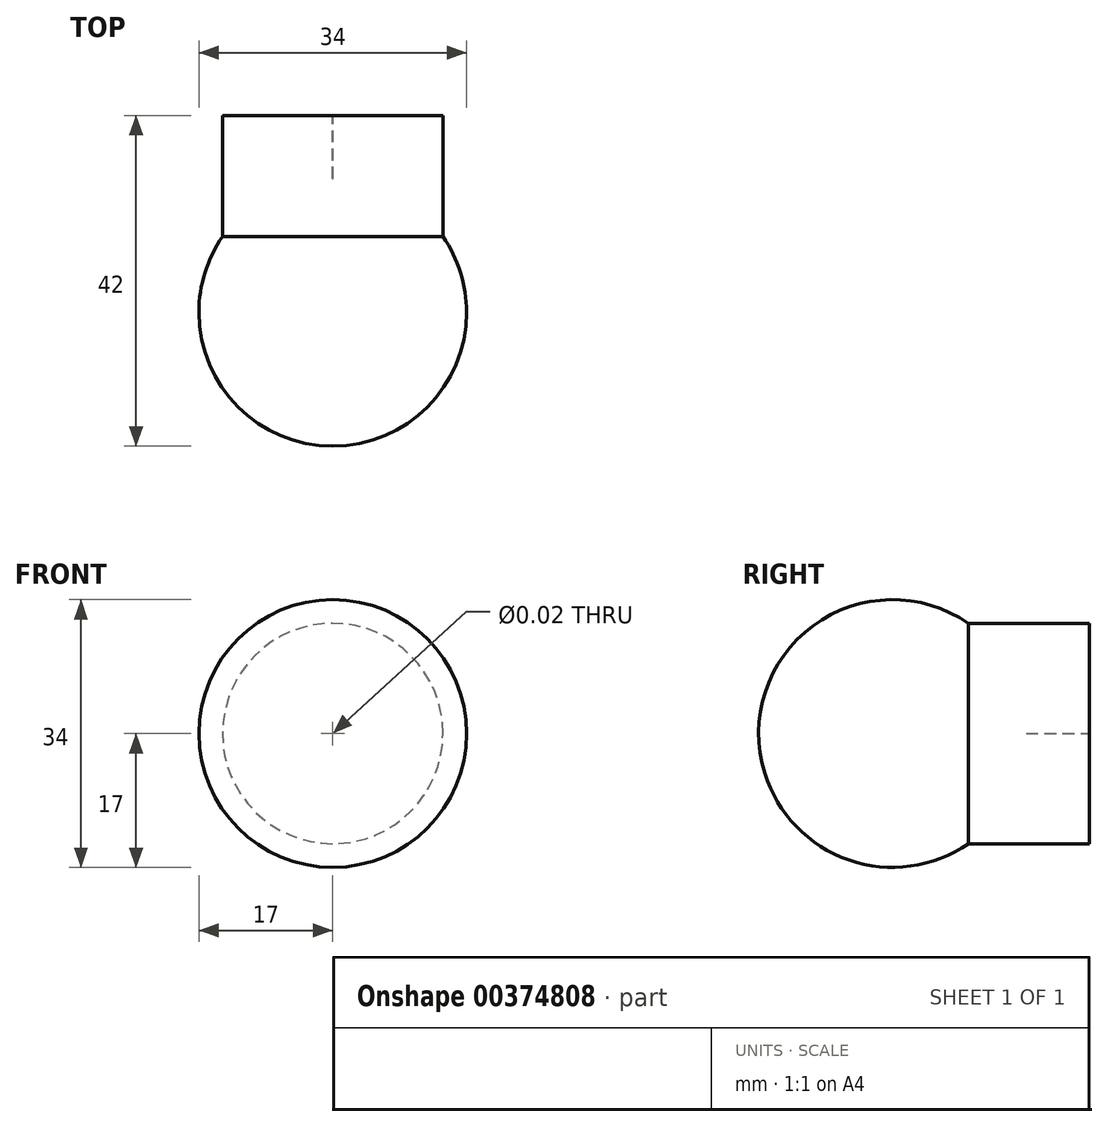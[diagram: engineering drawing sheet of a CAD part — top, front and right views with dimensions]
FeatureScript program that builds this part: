
annotation { "Feature Type Name" : "Feature", "Feature Type Description" : "" }
export const myFeature = defineFeature(function(context is Context, id is Id, definition is map)
    precondition{}
    {
        {
            var Q0;
            Q0=qCreatedBy(makeId("Front.planeOp"),FACE);
            var sketch = newSketch(context, id + "F0", { "sketchPlane" : qUnion([Q0])});
            skCircle(sketch, "E0", {"center": v(0, 0) * mm, "radius": 14 * mm});
            skCircle(sketch, "E1", {"center": v(0, 0) * mm, "radius": 11.6 * mm});
            skSolve(sketch);
        }
        {
            var Q0;
            Q0 = qSketchRegion(id + "F0", true);
            var Q1;
            Q1=makeQuery(id+"F0.imprint","IMPRINT",FACE,{"disambiguationData":[TD([[makeQuery(id+"F0.imprint","IMPRINT",EDGE,{"derivedFrom":sQuery(id+"F0.wireOp",EDGE,"E1")}),1.0]])]});
            extrude(context, id + "F1", {"entities" : qUnion([Q0, Q1]), "depth" : 25 * mm});
        }
        {
            var Q0;
            Q0=sQuery(id+"F0.wireOp",VERTEX,"E0.center");
            var Q1;
            Q1=makeQuery(id+"F1.opExtrude","SWEPT_BODY",BODY,{"disambiguationData":[OSD([sQuery(id+"F0.wireOp",EDGE,"E0")])]});
            hole(context, id + "F2", {"style" : HoleStyle.SIMPLE, "endStyle" : HoleEndStyle.BLIND, "oppositeDirection" : true, "standardTappedOrClearance" : lookupTablePath({ "standard" : "ANSI", "size" : "1/2 (0.5)", "type" : "Drilled" }), "standardBlindInLast" : lookupTablePath({ "standard" : "ANSI", "size" : "1/2", "type" : "Drilled" }), "holeDiameter" : 1 / 50.8 * mm, "holeDepth" : 14 * mm, "isTappedThrough" : true, "tappedDepth" : 12 * mm, "tapClearance" : 3, "locations" : qUnion([Q0]), "scope" : qUnion([Q1])});
        }
        {
            var Q0;
            Q0=makeQuery(id+"F1.opExtrude","CAP_FACE",FACE,{"disambiguationData":[OSD([sQuery(id+"F0.wireOp",EDGE,"E0")])],"isStart":false});
            var sketch = newSketch(context, id + "F3", { "sketchPlane" : qUnion([Q0])});
            skLineSegment(sketch, "E2", {"start": v(-17, 0) * mm, "end": v(17, 0) * mm});
            skArc(sketch, "E3", {"start": v(-17, 0) * mm, "mid": v(0, -17) * mm, "end": v(17, 0) * mm});
            skSolve(sketch);
        }
        {
            var Q0;
            {var subQ0=sQuery(id+"F3.wireOp",EDGE,"E3");Q0=makeQuery(id+"F3.imprint","IMPRINT",FACE,{"disambiguationData":[TD([[makeQuery(id+"F3.imprint","IMPRINT",EDGE,{"derivedFrom":subQ0}),1.0]])]});}
            var Q1;
            {var subQ0=sQuery(id+"F3.wireOp",EDGE,"E2");var subQ1=makeQuery(id+"F1.opExtrude","CAP_EDGE",EDGE,{"disambiguationData":[OSD([sQuery(id+"F0.wireOp",EDGE,"E0")])],"isStart":false});var subQ2=makeQuery(id+"F3.imprint","INTERSECT",VERTEX,{"disambiguationData":[OD(0.0)],"derivedFrom":[subQ1,subQ0]});Q1=makeQuery(id+"F3.imprint","IMPRINT",FACE,{"disambiguationData":[TD([[makeQuery(id+"F3.imprint","IMPRINT",EDGE,{"disambiguationData":[TD([[subQ2,-1.0]])],"derivedFrom":subQ0}),-1.0]])]});}
            var Q2;
            Q2=sQuery(id+"F3.wireOp",EDGE,"E2");
            revolve(context, id + "F4", {"operationType" : NewBodyOperationType.ADD, "entities" : qUnion([Q0, Q1]), "axis" : qUnion([Q2]), "revolveType" : RevolveType.FULL, "oppositeDirection" : true});
        }
    });
